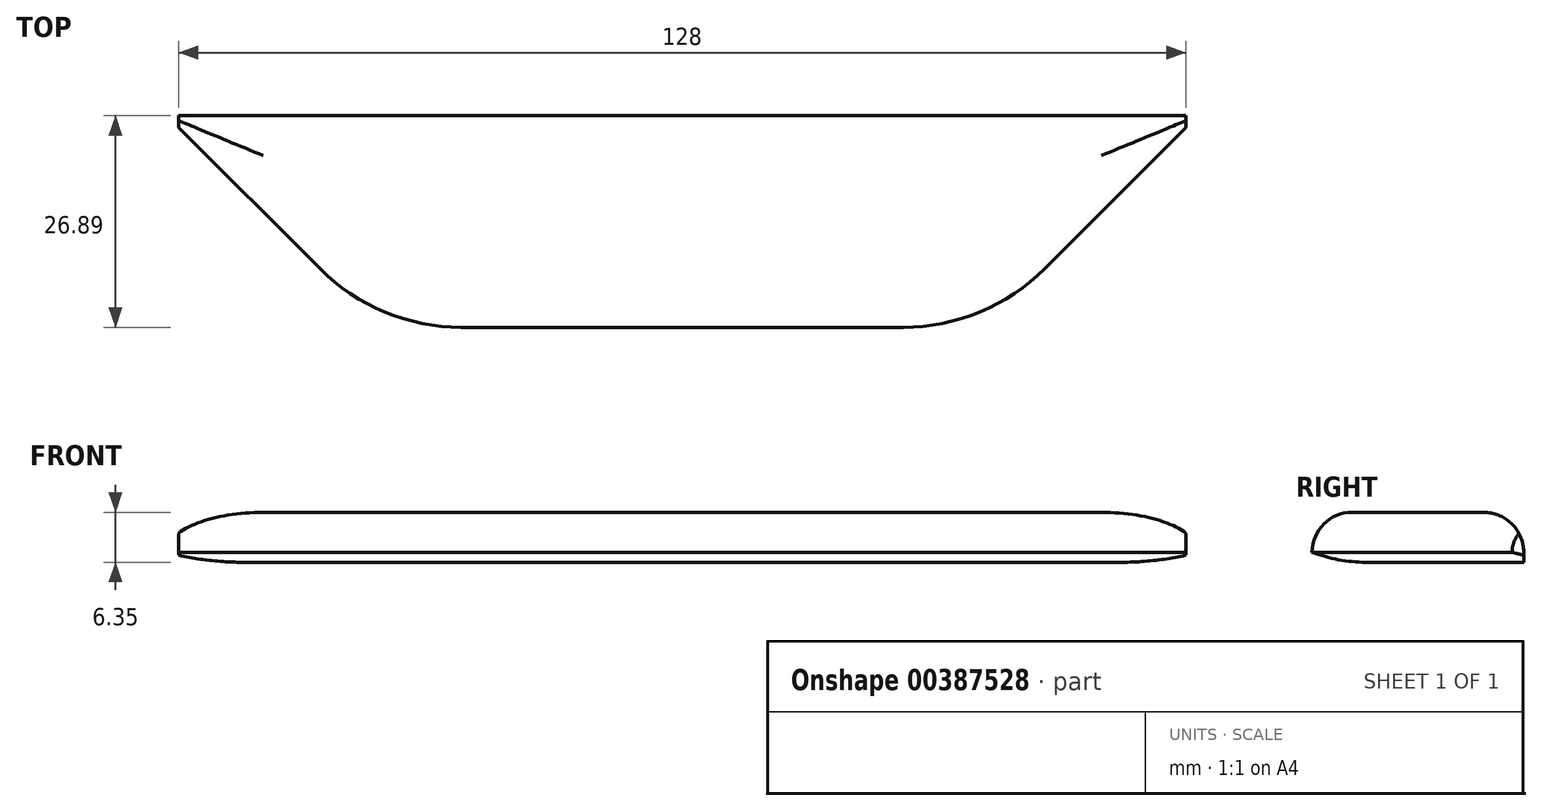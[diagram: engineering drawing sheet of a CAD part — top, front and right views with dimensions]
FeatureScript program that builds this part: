
annotation { "Feature Type Name" : "Feature", "Feature Type Description" : "" }
export const myFeature = defineFeature(function(context is Context, id is Id, definition is map)
    precondition{}
    {
        {
            var Q0;
            Q0=qCreatedBy(makeId("Top.planeOp"),FACE);
            var sketch = newSketch(context, id + "F0", { "sketchPlane" : qUnion([Q0])});
            skLineSegment(sketch, "E0.bottom", {"start": v(52.4, 33.55) * mm, "end": v(-75.6, 33.55) * mm});
            skLineSegment(sketch, "E0.top", {"start": v(52.4, 6.66) * mm, "end": v(-75.6, 6.66) * mm});
            skLineSegment(sketch, "E0.left", {"start": v(52.4, 33.55) * mm, "end": v(52.4, 6.66) * mm});
            skLineSegment(sketch, "E0.right", {"start": v(-75.6, 33.55) * mm, "end": v(-75.6, 6.66) * mm});
            skSolve(sketch);
        }
        {
            var Q0;
            Q0=makeQuery(id+"F0.imprint","IMPRINT",FACE,{"disambiguationData":[TD([[makeQuery(id+"F0.imprint","IMPRINT",EDGE,{"derivedFrom":sQuery(id+"F0.wireOp",EDGE,"E0.bottom")}),1.0]])]});
            extrude(context, id + "F1", {"entities" : qUnion([Q0]), "depth" : 6.35 * mm});
        }
        {
            var Q0;
            Q0=makeQuery(id+"F1.opExtrude","SWEPT_EDGE",EDGE,{"disambiguationData":[OSD([sQuery(id+"F0.wireOp",EDGE,"E0.top"),sQuery(id+"F0.wireOp",EDGE,"E0.right")])]});
            chamfer(context, id + "F2", {"entities" : qUnion([Q0]), "width" : 25.4 * mm, "tangentPropagation" : true});
        }
        {
            var Q0;
            Q0=makeQuery(id+"F1.opExtrude","SWEPT_EDGE",EDGE,{"disambiguationData":[OSD([sQuery(id+"F0.wireOp",EDGE,"E0.top"),sQuery(id+"F0.wireOp",EDGE,"E0.left")])]});
            chamfer(context, id + "F3", {"entities" : qUnion([Q0]), "width" : 25.4 * mm, "tangentPropagation" : true});
        }
        {
            var Q0;
            {var subQ0=sQuery(id+"F0.wireOp",EDGE,"E0.top");Q0=makeQuery(id+"F2.opChamfer","BLEND_EDGE",EDGE,{"blendedFrom":[makeQuery(id+"F1.opExtrude","SWEPT_EDGE",EDGE,{"disambiguationData":[OSD([subQ0,sQuery(id+"F0.wireOp",EDGE,"E0.right")])]}),makeQuery(id+"F1.opExtrude","SWEPT_FACE",FACE,{"disambiguationData":[OSD([subQ0])]})],"blendedInto":[makeQuery(id+"F1.opExtrude","SWEPT_FACE",FACE,{"disambiguationData":[OSD([subQ0])]})]});}
            fillet(context, id + "F4", {"entities" : qUnion([Q0]), "radius" : 25.4 * mm, "tangentPropagation" : true, "allowEdgeOverflow" : false});
        }
        {
            var Q0;
            {var subQ0=sQuery(id+"F0.wireOp",EDGE,"E0.top");Q0=makeQuery(id+"F3.opChamfer","BLEND_EDGE",EDGE,{"blendedFrom":[makeQuery(id+"F1.opExtrude","SWEPT_EDGE",EDGE,{"disambiguationData":[OSD([subQ0,sQuery(id+"F0.wireOp",EDGE,"E0.left")])]}),makeQuery(id+"F1.opExtrude","SWEPT_FACE",FACE,{"disambiguationData":[OSD([subQ0])]})],"blendedInto":[makeQuery(id+"F1.opExtrude","SWEPT_FACE",FACE,{"disambiguationData":[OSD([subQ0])]})]});}
            fillet(context, id + "F5", {"entities" : qUnion([Q0]), "radius" : 25.4 * mm, "tangentPropagation" : true, "allowEdgeOverflow" : false});
        }
        {
            var Q0;
            Q0=makeQuery(id+"F1.opExtrude","CAP_FACE",FACE,{"disambiguationData":[OSD([sQuery(id+"F0.wireOp",EDGE,"E0.bottom"),sQuery(id+"F0.wireOp",EDGE,"E0.top"),sQuery(id+"F0.wireOp",EDGE,"E0.left"),sQuery(id+"F0.wireOp",EDGE,"E0.right")])],"isStart":false});
            fillet(context, id + "F6", {"entities" : qUnion([Q0]), "radius" : 5.08 * mm, "tangentPropagation" : true, "allowEdgeOverflow" : false});
        }
        {
            var Q0;
            {var subQ0=sQuery(id+"F0.wireOp",EDGE,"E0.left");var subQ1=sQuery(id+"F0.wireOp",EDGE,"E0.top");Q0=makeQuery(id+"F3.opChamfer","BLEND_EDGE",EDGE,{"blendedFrom":[makeQuery(id+"F1.opExtrude","SWEPT_EDGE",EDGE,{"disambiguationData":[OSD([subQ1,subQ0])]}),makeQuery(id+"F1.opExtrude","CAP_FACE",FACE,{"disambiguationData":[OSD([sQuery(id+"F0.wireOp",EDGE,"E0.bottom"),subQ1,subQ0,sQuery(id+"F0.wireOp",EDGE,"E0.right")])],"isStart":true})],"blendedInto":[makeQuery(id+"F1.opExtrude","CAP_FACE",FACE,{"disambiguationData":[OSD([sQuery(id+"F0.wireOp",EDGE,"E0.bottom"),subQ1,subQ0,sQuery(id+"F0.wireOp",EDGE,"E0.right")])],"isStart":true})]});}
            var Q1;
            {var subQ0=sQuery(id+"F0.wireOp",EDGE,"E0.right");var subQ1=sQuery(id+"F0.wireOp",EDGE,"E0.top");Q1=makeQuery(id+"F2.opChamfer","BLEND_EDGE",EDGE,{"blendedFrom":[makeQuery(id+"F1.opExtrude","SWEPT_EDGE",EDGE,{"disambiguationData":[OSD([subQ1,subQ0])]}),makeQuery(id+"F1.opExtrude","CAP_FACE",FACE,{"disambiguationData":[OSD([sQuery(id+"F0.wireOp",EDGE,"E0.bottom"),subQ1,sQuery(id+"F0.wireOp",EDGE,"E0.left"),subQ0])],"isStart":true})],"blendedInto":[makeQuery(id+"F1.opExtrude","CAP_FACE",FACE,{"disambiguationData":[OSD([sQuery(id+"F0.wireOp",EDGE,"E0.bottom"),subQ1,sQuery(id+"F0.wireOp",EDGE,"E0.left"),subQ0])],"isStart":true})]});}
            var Q2;
            {var subQ0=sQuery(id+"F0.wireOp",EDGE,"E0.left");var subQ1=sQuery(id+"F0.wireOp",EDGE,"E0.top");Q2=makeQuery(id+"F5.opFillet","BLEND_EDGE",EDGE,{"blendedFrom":[makeQuery(id+"F3.opChamfer","BLEND_EDGE",EDGE,{"blendedFrom":[makeQuery(id+"F1.opExtrude","SWEPT_EDGE",EDGE,{"disambiguationData":[OSD([subQ1,subQ0])]}),makeQuery(id+"F1.opExtrude","SWEPT_FACE",FACE,{"disambiguationData":[OSD([subQ1])]})],"blendedInto":[makeQuery(id+"F1.opExtrude","SWEPT_FACE",FACE,{"disambiguationData":[OSD([subQ1])]})]}),makeQuery(id+"F1.opExtrude","CAP_FACE",FACE,{"disambiguationData":[OSD([sQuery(id+"F0.wireOp",EDGE,"E0.bottom"),subQ1,subQ0,sQuery(id+"F0.wireOp",EDGE,"E0.right")])],"isStart":true})],"blendedInto":[makeQuery(id+"F1.opExtrude","CAP_FACE",FACE,{"disambiguationData":[OSD([sQuery(id+"F0.wireOp",EDGE,"E0.bottom"),subQ1,subQ0,sQuery(id+"F0.wireOp",EDGE,"E0.right")])],"isStart":true})]});}
            var Q3;
            {var subQ0=sQuery(id+"F0.wireOp",EDGE,"E0.right");var subQ1=sQuery(id+"F0.wireOp",EDGE,"E0.top");Q3=makeQuery(id+"F4.opFillet","BLEND_EDGE",EDGE,{"blendedFrom":[makeQuery(id+"F2.opChamfer","BLEND_EDGE",EDGE,{"blendedFrom":[makeQuery(id+"F1.opExtrude","SWEPT_EDGE",EDGE,{"disambiguationData":[OSD([subQ1,subQ0])]}),makeQuery(id+"F1.opExtrude","SWEPT_FACE",FACE,{"disambiguationData":[OSD([subQ1])]})],"blendedInto":[makeQuery(id+"F1.opExtrude","SWEPT_FACE",FACE,{"disambiguationData":[OSD([subQ1])]})]}),makeQuery(id+"F1.opExtrude","CAP_FACE",FACE,{"disambiguationData":[OSD([sQuery(id+"F0.wireOp",EDGE,"E0.bottom"),subQ1,sQuery(id+"F0.wireOp",EDGE,"E0.left"),subQ0])],"isStart":true})],"blendedInto":[makeQuery(id+"F1.opExtrude","CAP_FACE",FACE,{"disambiguationData":[OSD([sQuery(id+"F0.wireOp",EDGE,"E0.bottom"),subQ1,sQuery(id+"F0.wireOp",EDGE,"E0.left"),subQ0])],"isStart":true})]});}
            fillet(context, id + "F7", {"entities" : qUnion([Q0, Q1, Q2, Q3]), "radius" : 19.05 * mm, "tangentPropagation" : true, "allowEdgeOverflow" : false});
        }
    });
